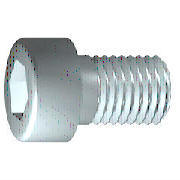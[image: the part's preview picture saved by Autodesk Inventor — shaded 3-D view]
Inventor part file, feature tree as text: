
AUTODESK INVENTOR PART (.ipt)
format: ipt  version: 2013 (Build 170138000, 138)  size: 173,568 bytes
history: native  units: mm (DEFAULTED — no unit token found)
features: sketch x2, extrude x1, plane x1, fillet x1
ambient origin geometry x7: Origin, YZ Plane, XY Plane, X Axis, Y Axis, Z Axis, Center Point
bodies: Solid1 (feature_tree), Body (feature_tree)
feature tree (5):
  extrude  "Slot"  Depth=0.766912mm
  plane  "Work Plane1"
  fillet  "Fillet2"  Radius=8.0mm
  sketch  "Sketch1"  dims[d1=28.0mm d2=0.766912mm d3=8.0mm]
  sketch  "Sketch2"  dims[d4=4.0mm d5=60.0deg d6=8.0mm d7=8.0mm d8=6.928203mm d9=13.0mm d10=90.0deg d11=10.0mm d12=0.0mm d13=28.0mm d14=0.0mm d15=0.766812mm d16=0.766813mm d17=0.8mm d19=0.0mm d26=200.0mm d27=45.0deg d28=0.0mm d29=0.0mm d30=0.1mm]
